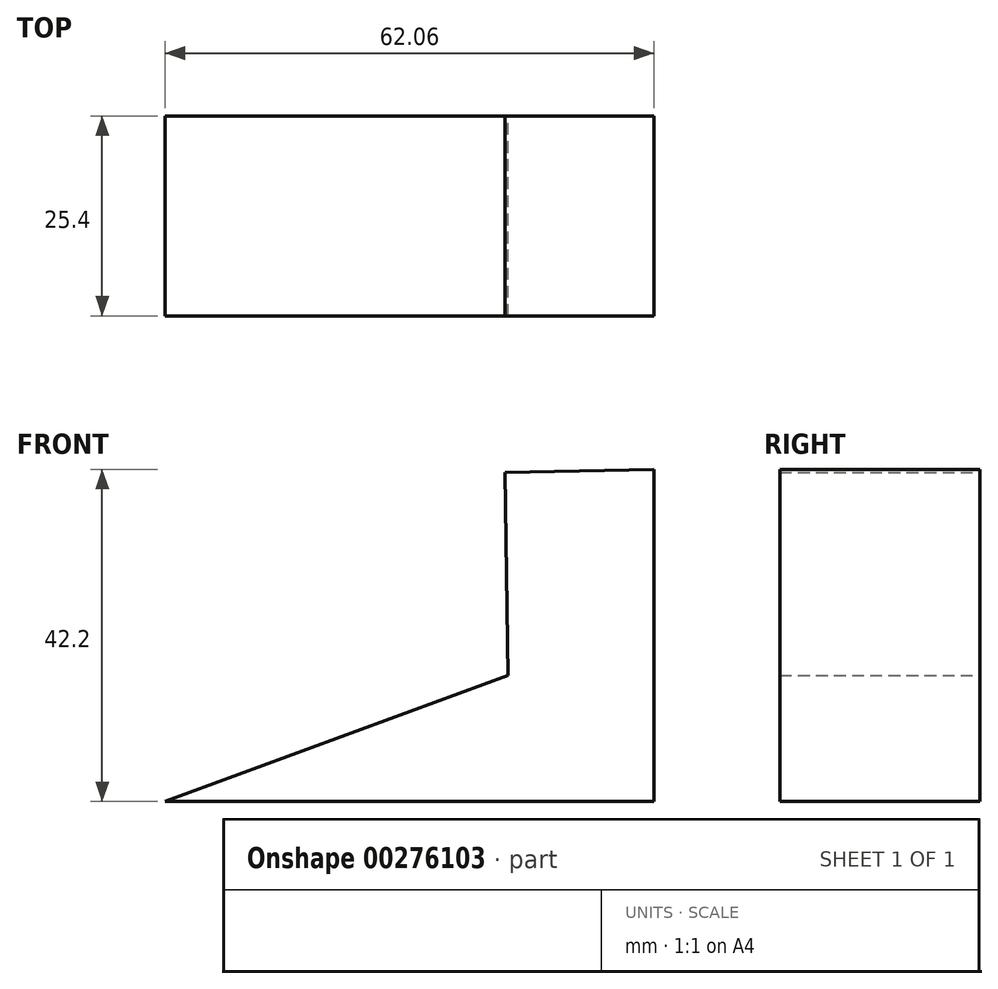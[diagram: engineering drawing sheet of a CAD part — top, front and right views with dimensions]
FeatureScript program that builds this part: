
annotation { "Feature Type Name" : "Feature", "Feature Type Description" : "" }
export const myFeature = defineFeature(function(context is Context, id is Id, definition is map)
    precondition{}
    {
        {
            var Q0;
            Q0=qCreatedBy(makeId("Front.planeOp"),FACE);
            var sketch = newSketch(context, id + "F0", { "sketchPlane" : qUnion([Q0])});
            skLineSegment(sketch, "E0", {"start": v(0, 42.2) * mm, "end": v(0, 0) * mm});
            skLineSegment(sketch, "E1", {"start": v(0, 0) * mm, "end": v(-37.43, 0) * mm});
            skLineSegment(sketch, "E2", {"start": v(-37.43, 0) * mm, "end": v(-62.06, 0) * mm});
            skLineSegment(sketch, "E3", {"start": v(-62.06, 0) * mm, "end": v(-18.52, 16.04) * mm});
            skLineSegment(sketch, "E4", {"start": v(-18.9, 41.82) * mm, "end": v(0, 42.2) * mm});
            skLineSegment(sketch, "E5", {"start": v(-18.9, 41.82) * mm, "end": v(-18.52, 16.04) * mm});
            skSolve(sketch);
        }
        {
            var Q0;
            Q0 = qSketchRegion(id + "F0", true);
            extrude(context, id + "F1", {"entities" : qUnion([Q0]), "depth" : 25.4 * mm});
        }
    });
